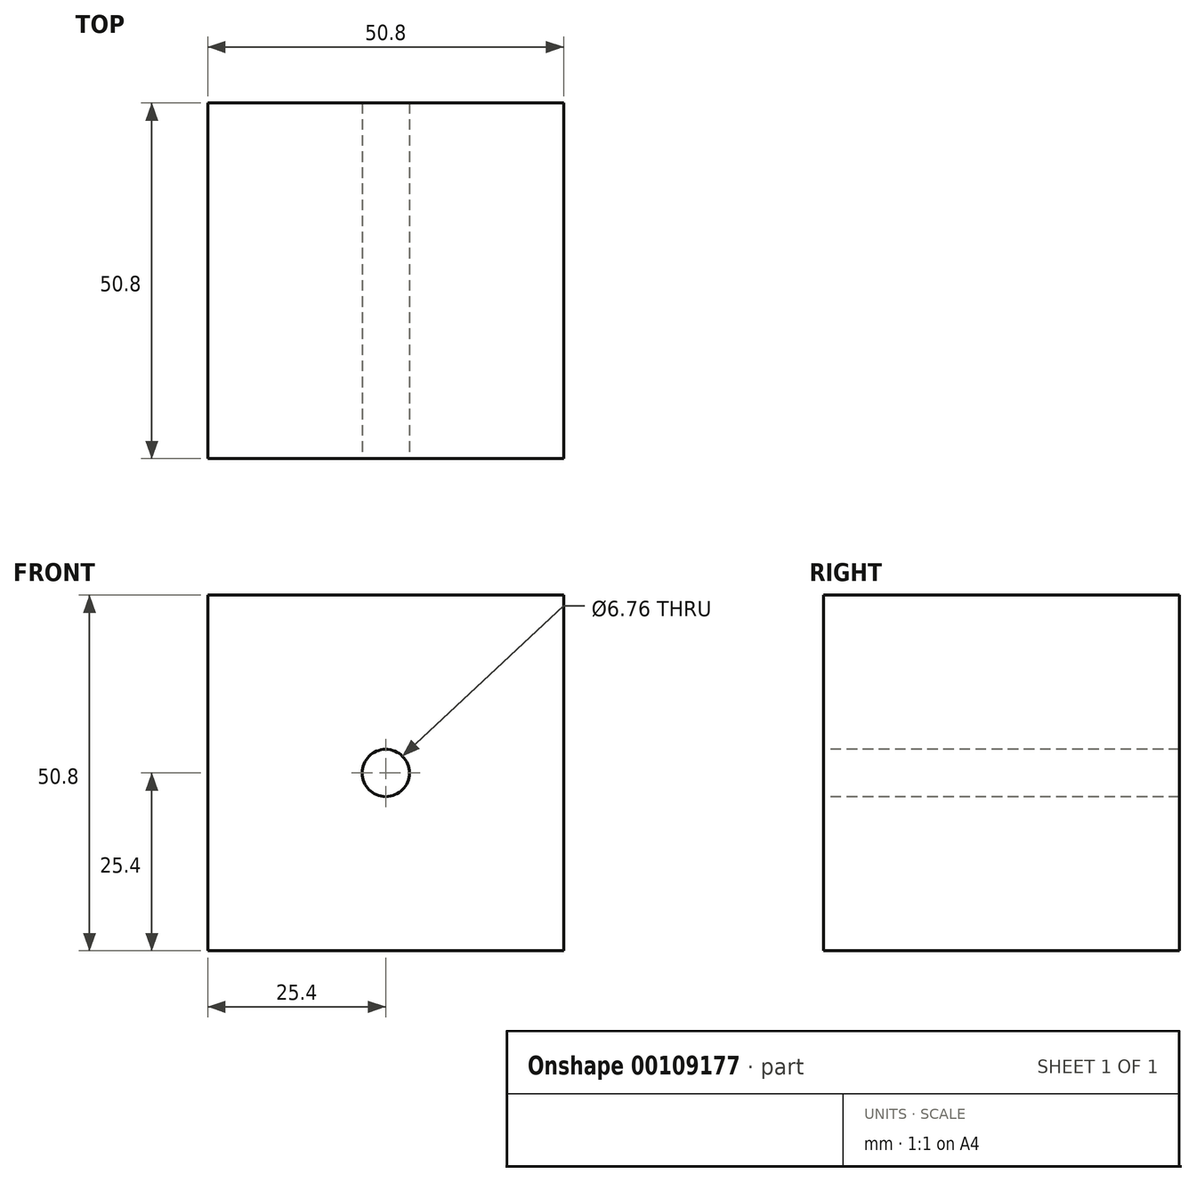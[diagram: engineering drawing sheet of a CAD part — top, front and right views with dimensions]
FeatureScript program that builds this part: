
annotation { "Feature Type Name" : "Feature", "Feature Type Description" : "" }
export const myFeature = defineFeature(function(context is Context, id is Id, definition is map)
    precondition{}
    {
        {
            var Q0;
            Q0=qCreatedBy(makeId("Top.planeOp"),FACE);
            var sketch = newSketch(context, id + "F0", { "sketchPlane" : qUnion([Q0])});
            skLineSegment(sketch, "E0.bottom", {"start": v(0, 0) * mm, "end": v(50.8, 0) * mm});
            skLineSegment(sketch, "E0.top", {"start": v(0, 50.8) * mm, "end": v(50.8, 50.8) * mm});
            skLineSegment(sketch, "E0.left", {"start": v(0, 0) * mm, "end": v(0, 50.8) * mm});
            skLineSegment(sketch, "E0.right", {"start": v(50.8, 0) * mm, "end": v(50.8, 50.8) * mm});
            skSolve(sketch);
        }
        {
            var Q0;
            Q0=makeQuery(id+"F0.imprint","IMPRINT",FACE,{"disambiguationData":[TD([[makeQuery(id+"F0.imprint","IMPRINT",EDGE,{"derivedFrom":sQuery(id+"F0.wireOp",EDGE,"E0.bottom")}),1.0]])]});
            extrude(context, id + "F1", {"entities" : qUnion([Q0]), "depth" : 50.8 * mm});
        }
        {
            var Q0;
            Q0=makeQuery(id+"F1.opExtrude","SWEPT_FACE",FACE,{"disambiguationData":[OSD([sQuery(id+"F0.wireOp",EDGE,"E0.bottom")])]});
            var sketch = newSketch(context, id + "F2", { "sketchPlane" : qUnion([Q0])});
            skPoint(sketch, "E1", {"position": v(25.4, 25.4) * mm});
            skSolve(sketch);
        }
        {
            var Q0;
            Q0=sQuery(id+"F2.wireOp",VERTEX,"E1");
            var Q1;
            Q1=makeQuery(id+"F1.opExtrude","SWEPT_BODY",BODY,{"disambiguationData":[OSD([sQuery(id+"F0.wireOp",EDGE,"E0.bottom"),sQuery(id+"F0.wireOp",EDGE,"E0.top"),sQuery(id+"F0.wireOp",EDGE,"E0.left"),sQuery(id+"F0.wireOp",EDGE,"E0.right")])]});
            hole(context, id + "F3", {"style" : HoleStyle.SIMPLE, "endStyle" : HoleEndStyle.THROUGH, "standardTappedOrClearance" : lookupTablePath({ "standard" : "ANSI", "fit" : "Normal (ASME)", "size" : "1/4", "type" : "Clearance" }), "standardBlindInLast" : lookupTablePath({ "fit" : "Free", "standard" : "ANSI", "size" : "1/4", "type" : "Clearance" }), "holeDiameter" : 6.76 * mm, "locations" : qUnion([Q0]), "scope" : qUnion([Q1]), "isTappedThrough" : true});
        }
    });
